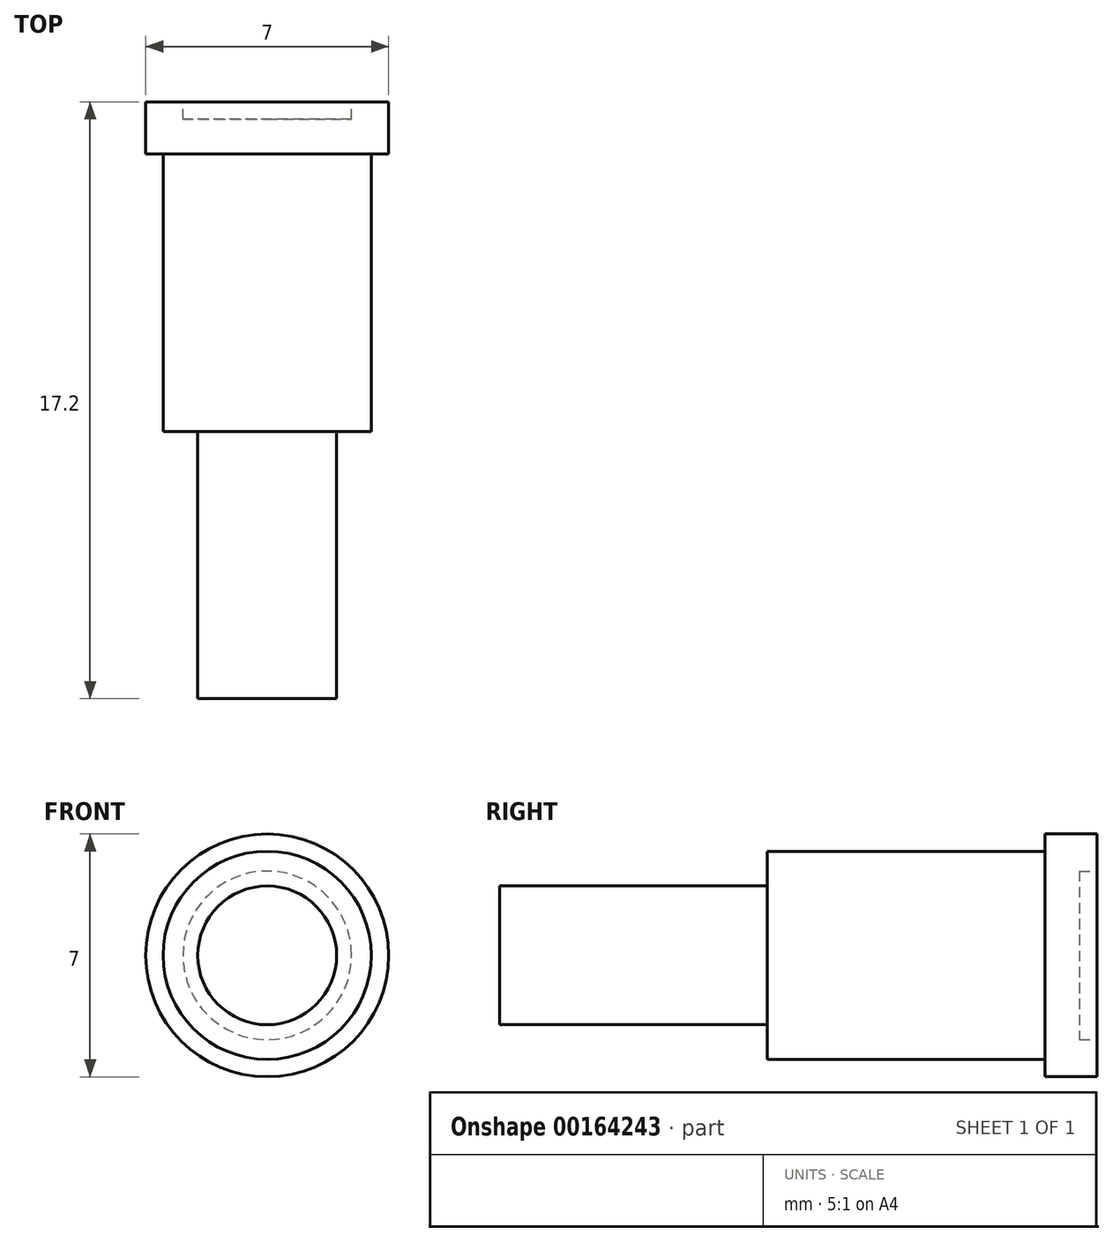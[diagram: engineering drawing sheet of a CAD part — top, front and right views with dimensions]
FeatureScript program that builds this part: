
annotation { "Feature Type Name" : "Feature", "Feature Type Description" : "" }
export const myFeature = defineFeature(function(context is Context, id is Id, definition is map)
    precondition{}
    {
        {
            var Q0;
            Q0=qCreatedBy(makeId("Front.planeOp"),FACE);
            var sketch = newSketch(context, id + "F0", { "sketchPlane" : qUnion([Q0])});
            skCircle(sketch, "E0", {"center": v(-14.26, 19.5) * mm, "radius": 3.5 * mm});
            skSolve(sketch);
        }
        {
            var Q0;
            Q0 = qSketchRegion(id + "F0", true);
            extrude(context, id + "F1", {"entities" : qUnion([Q0]), "depth" : 1.5 * mm});
        }
        {
            var Q0;
            Q0=makeQuery(id+"F1.opExtrude","CAP_FACE",FACE,{"disambiguationData":[OSD([sQuery(id+"F0.wireOp",EDGE,"E0")])],"isStart":false});
            var sketch = newSketch(context, id + "F2", { "sketchPlane" : qUnion([Q0])});
            skCircle(sketch, "E1", {"center": v(-14.26, 19.5) * mm, "radius": 3 * mm});
            skSolve(sketch);
        }
        {
            var Q0;
            Q0 = qSketchRegion(id + "F2", true);
            extrude(context, id + "F3", {"entities" : qUnion([Q0]), "operationType" : NewBodyOperationType.ADD, "depth" : 8 * mm});
        }
        {
            var Q0;
            Q0=makeQuery(id+"F3.opExtrude","CAP_FACE",FACE,{"disambiguationData":[OSD([sQuery(id+"F2.wireOp",EDGE,"E1")])],"isStart":false});
            var sketch = newSketch(context, id + "F4", { "sketchPlane" : qUnion([Q0])});
            skCircle(sketch, "E2", {"center": v(-14.26, 19.5) * mm, "radius": 2 * mm});
            skSolve(sketch);
        }
        {
            var Q0;
            Q0 = qSketchRegion(id + "F4", true);
            extrude(context, id + "F5", {"entities" : qUnion([Q0]), "operationType" : NewBodyOperationType.ADD, "depth" : 7.7 * mm});
        }
        {
            var Q0;
            Q0=makeQuery(id+"F1.opExtrude","CAP_FACE",FACE,{"disambiguationData":[OSD([sQuery(id+"F0.wireOp",EDGE,"E0")])],"isStart":true});
            var sketch = newSketch(context, id + "F6", { "sketchPlane" : qUnion([Q0])});
            skCircle(sketch, "E3", {"center": v(14.26, 19.5) * mm, "radius": 2.43 * mm});
            skSolve(sketch);
        }
        {
            var Q0;
            Q0 = qSketchRegion(id + "F6", true);
            extrude(context, id + "F7", {"entities" : qUnion([Q0]), "operationType" : NewBodyOperationType.REMOVE, "oppositeDirection" : true, "depth" : .5 * mm});
        }
    });
